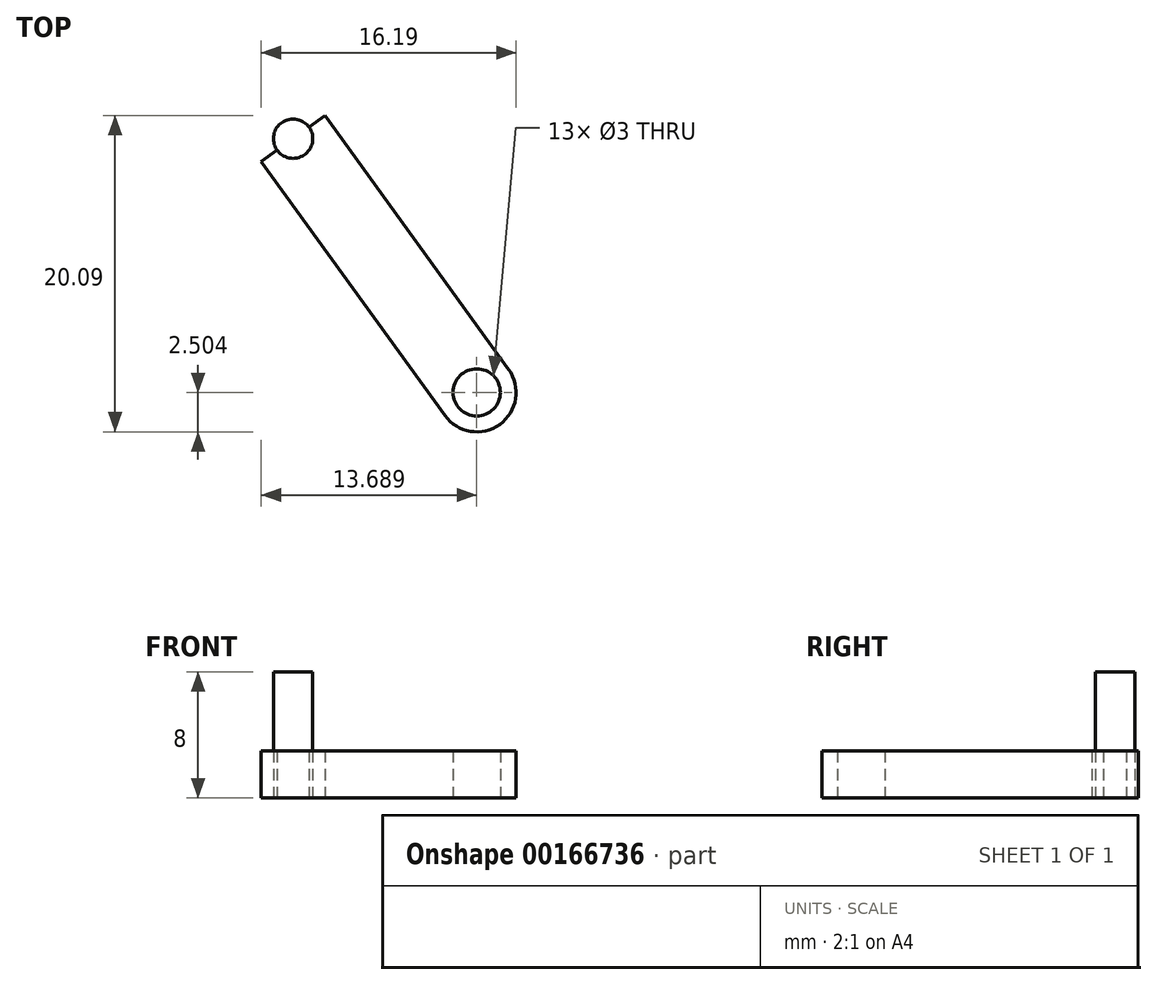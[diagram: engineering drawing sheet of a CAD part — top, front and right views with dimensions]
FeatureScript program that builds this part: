
annotation { "Feature Type Name" : "Feature", "Feature Type Description" : "" }
export const myFeature = defineFeature(function(context is Context, id is Id, definition is map)
    precondition{}
    {
        {
            var Q0;
            Q0=qCreatedBy(makeId("Top.planeOp"),FACE);
            var sketch = newSketch(context, id + "F0", { "sketchPlane" : qUnion([Q0])});
            skLineSegment(sketch, "E0", {"start": v(-2.66, 9.09) * mm, "end": v(9, -7.03) * mm});
            skLineSegment(sketch, "E1", {"start": v(9, -7.03) * mm, "end": v(4.95, -9.96) * mm});
            skLineSegment(sketch, "E2", {"start": v(4.95, -9.96) * mm, "end": v(-6.7, 6.16) * mm});
            skLineSegment(sketch, "E3", {"start": v(-6.7, 6.16) * mm, "end": v(-2.66, 9.09) * mm});
            skPoint(sketch, "E4", {"position": v(-4.68, 7.62) * mm});
            skPoint(sketch, "E5", {"position": v(6.98, -8.5) * mm});
            skCircle(sketch, "E6", {"center": v(6.98, -8.5) * mm, "radius": 2.5 * mm});
            skCircle(sketch, "E7", {"center": v(-4.68, 7.62) * mm, "radius": 1.25 * mm});
            skCircle(sketch, "E8", {"center": v(6.98, -8.5) * mm, "radius": 1.5 * mm});
            skSolve(sketch);
        }
        {
            var Q0;
            Q0 = qSketchRegion(id + "F0", true);
            extrude(context, id + "F1", {"entities" : qUnion([Q0]), "depth" : 3 * mm});
        }
        {
            var Q0;
            {var subQ0=sQuery(id+"F0.wireOp",EDGE,"E7");var subQ1=sQuery(id+"F0.wireOp",EDGE,"E3");var subQ2=makeQuery(id+"F0.imprint","INTERSECT",VERTEX,{"disambiguationData":[OD(0.0)],"derivedFrom":[subQ1,subQ0]});Q0=makeQuery(id+"F0.imprint","IMPRINT",FACE,{"disambiguationData":[TD([[makeQuery(id+"F0.imprint","IMPRINT",EDGE,{"disambiguationData":[TD([[subQ2,-1.0]])],"derivedFrom":subQ1}),-1.0]])]});}
            var Q1;
            {var subQ0=sQuery(id+"F0.wireOp",EDGE,"E7");var subQ1=sQuery(id+"F0.wireOp",EDGE,"E3");var subQ2=makeQuery(id+"F0.imprint","INTERSECT",VERTEX,{"disambiguationData":[OD(0.0)],"derivedFrom":[subQ1,subQ0]});Q1=makeQuery(id+"F0.imprint","IMPRINT",FACE,{"disambiguationData":[TD([[makeQuery(id+"F0.imprint","IMPRINT",EDGE,{"disambiguationData":[TD([[subQ2,-1.0]])],"derivedFrom":subQ1}),1.0]])]});}
            extrude(context, id + "F2", {"entities" : qUnion([Q0, Q1]), "depth" : 8 * mm});
        }
    });
